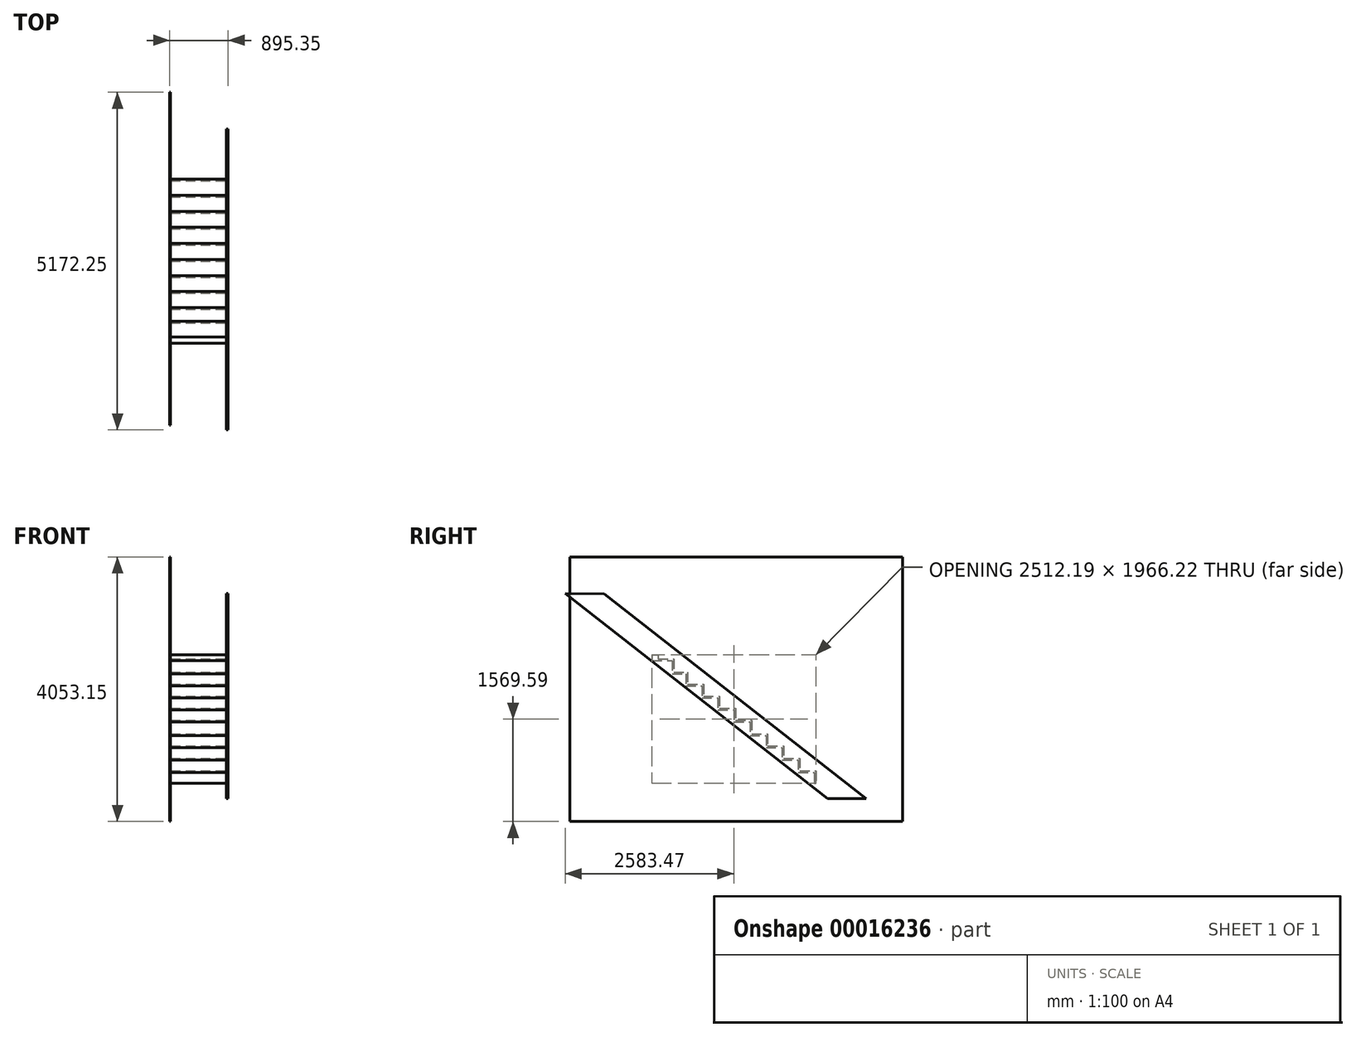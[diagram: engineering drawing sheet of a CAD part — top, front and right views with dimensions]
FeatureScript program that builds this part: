
annotation { "Feature Type Name" : "Feature", "Feature Type Description" : "" }
export const myFeature = defineFeature(function(context is Context, id is Id, definition is map)
    precondition{}
    {
        {
            var Q0;
            Q0=qCreatedBy(makeId("Right.planeOp"),FACE);
            var sketch = newSketch(context, id + "F0", { "sketchPlane" : qUnion([Q0])});
            skLineSegment(sketch, "E0", {"start": v(-670.58, 605.84) * mm, "end": v(-454.68, 605.84) * mm});
            skLineSegment(sketch, "E1", {"start": v(-454.68, 605.84) * mm, "end": v(-454.68, 402.64) * mm});
            skLineSegment(sketch, "E2", {"start": v(-454.68, 402.64) * mm, "end": v(-245.13, 402.64) * mm});
            skLineSegment(sketch, "E3", {"start": v(-245.13, 402.64) * mm, "end": v(-245.13, 218.5) * mm});
            skLineSegment(sketch, "E4", {"start": v(-245.13, 218.5) * mm, "end": v(0.68, 218.5) * mm});
            skLineSegment(sketch, "E5", {"start": v(0.68, 218.5) * mm, "end": v(0.68, 34.34) * mm});
            skLineSegment(sketch, "E6", {"start": v(0.68, 34.34) * mm, "end": v(246.48, 34.34) * mm});
            skLineSegment(sketch, "E7", {"start": v(246.48, 34.34) * mm, "end": v(246.48, -149.8) * mm});
            skLineSegment(sketch, "E8", {"start": v(246.48, -149.8) * mm, "end": v(492.28, -149.8) * mm});
            skLineSegment(sketch, "E9", {"start": v(492.28, -149.8) * mm, "end": v(492.28, -333.96) * mm});
            skLineSegment(sketch, "E10", {"start": v(492.28, -333.96) * mm, "end": v(738.09, -333.96) * mm});
            skLineSegment(sketch, "E11", {"start": v(738.09, -333.96) * mm, "end": v(738.09, -543.18) * mm});
            skLineSegment(sketch, "E12", {"start": v(-772.64, 715.75) * mm, "end": v(-772.64, -717.04) * mm, "construction": true});
            skLineSegment(sketch, "E13", {"start": v(-833.07, 660.16) * mm, "end": v(734.14, -564.28) * mm});
            skLineSegment(sketch, "E14.0", {"start": v(763.16, -308.88) * mm, "end": v(763.16, -518.1) * mm});
            skLineSegment(sketch, "E14.1", {"start": v(517.36, -308.88) * mm, "end": v(763.16, -308.88) * mm});
            skLineSegment(sketch, "E14.2", {"start": v(-220.05, 427.72) * mm, "end": v(-220.05, 243.57) * mm});
            skLineSegment(sketch, "E14.3", {"start": v(-429.6, 427.72) * mm, "end": v(-220.05, 427.72) * mm});
            skLineSegment(sketch, "E14.4", {"start": v(-429.6, 630.92) * mm, "end": v(-429.6, 427.72) * mm});
            skLineSegment(sketch, "E14.5", {"start": v(-670.58, 630.92) * mm, "end": v(-429.6, 630.92) * mm});
            skLineSegment(sketch, "E14.6", {"start": v(-220.05, 243.57) * mm, "end": v(25.75, 243.57) * mm});
            skLineSegment(sketch, "E14.7", {"start": v(25.75, 243.57) * mm, "end": v(25.75, 59.42) * mm});
            skLineSegment(sketch, "E14.8", {"start": v(25.75, 59.42) * mm, "end": v(271.55, 59.42) * mm});
            skLineSegment(sketch, "E14.9", {"start": v(271.55, 59.42) * mm, "end": v(271.55, -124.73) * mm});
            skLineSegment(sketch, "E14.10", {"start": v(271.55, -124.73) * mm, "end": v(517.36, -124.73) * mm});
            skLineSegment(sketch, "E14.11", {"start": v(517.36, -124.73) * mm, "end": v(517.36, -308.88) * mm});
            skLineSegment(sketch, "E15.bottom", {"start": v(-765.83, 694.74) * mm, "end": v(-670.58, 694.74) * mm});
            skLineSegment(sketch, "E15.top", {"start": v(-765.83, 605.84) * mm, "end": v(-670.58, 605.84) * mm});
            skLineSegment(sketch, "E15.left", {"start": v(-765.83, 694.74) * mm, "end": v(-765.83, 605.84) * mm});
            skLineSegment(sketch, "E15.right", {"start": v(-670.58, 694.74) * mm, "end": v(-670.58, 630.92) * mm});
            skLineSegment(sketch, "E16", {"start": v(763.16, -518.1) * mm, "end": v(1008.96, -518.1) * mm});
            skLineSegment(sketch, "E17", {"start": v(1008.96, -518.1) * mm, "end": v(1008.96, -697.8) * mm});
            skLineSegment(sketch, "E18", {"start": v(1008.96, -697.8) * mm, "end": v(1254.76, -697.8) * mm});
            skLineSegment(sketch, "E19", {"start": v(1254.76, -697.8) * mm, "end": v(1254.76, -887.85) * mm});
            skLineSegment(sketch, "E20", {"start": v(1254.76, -887.85) * mm, "end": v(1500.56, -887.85) * mm});
            skLineSegment(sketch, "E21", {"start": v(1500.56, -887.85) * mm, "end": v(1500.56, -1083.23) * mm});
            skLineSegment(sketch, "E22", {"start": v(1500.56, -1083.23) * mm, "end": v(1746.37, -1083.23) * mm});
            skLineSegment(sketch, "E23", {"start": v(1746.37, -1083.23) * mm, "end": v(1746.37, -1271.48) * mm});
            skLineSegment(sketch, "E24.0", {"start": v(1721.3, -1108.3) * mm, "end": v(1721.3, -1271.48) * mm});
            skLineSegment(sketch, "E24.1", {"start": v(1475.5, -1108.3) * mm, "end": v(1721.3, -1108.3) * mm});
            skLineSegment(sketch, "E24.2", {"start": v(1475.5, -912.92) * mm, "end": v(1475.5, -1108.3) * mm});
            skLineSegment(sketch, "E24.3", {"start": v(1229.7, -912.92) * mm, "end": v(1475.5, -912.92) * mm});
            skLineSegment(sketch, "E24.4", {"start": v(738.09, -543.18) * mm, "end": v(983.89, -543.18) * mm});
            skLineSegment(sketch, "E24.5", {"start": v(983.89, -543.18) * mm, "end": v(983.89, -722.86) * mm});
            skLineSegment(sketch, "E24.6", {"start": v(983.89, -722.86) * mm, "end": v(1229.7, -722.86) * mm});
            skLineSegment(sketch, "E24.7", {"start": v(1229.7, -722.86) * mm, "end": v(1229.7, -912.92) * mm});
            skLineSegment(sketch, "E25", {"start": v(1721.3, -1271.48) * mm, "end": v(1746.37, -1271.48) * mm});
            skSolve(sketch);
        }
        {
            var Q0;
            {var subQ5=sQuery(id+"F0.wireOp",EDGE,"E0");Q0=makeQuery(id+"F0.imprint","IMPRINT",FACE,{"disambiguationData":[TD([[makeQuery(id+"F0.imprint","IMPRINT",EDGE,{"derivedFrom":subQ5}),1.0]])]});}
            extrude(context, id + "F1", {"entities" : qUnion([Q0]), "oppositeDirection" : true, "depth" : 857.25 * mm});
        }
        {
            var Q0;
            Q0=makeQuery(id+"F1.opExtrude","CAP_FACE",FACE,{"disambiguationData":[OSD([sQuery(id+"F0.wireOp",EDGE,"E0"),sQuery(id+"F0.wireOp",EDGE,"E1"),sQuery(id+"F0.wireOp",EDGE,"E2"),sQuery(id+"F0.wireOp",EDGE,"E3"),sQuery(id+"F0.wireOp",EDGE,"E4"),sQuery(id+"F0.wireOp",EDGE,"E5"),sQuery(id+"F0.wireOp",EDGE,"E6"),sQuery(id+"F0.wireOp",EDGE,"E7"),sQuery(id+"F0.wireOp",EDGE,"E8"),sQuery(id+"F0.wireOp",EDGE,"E9"),sQuery(id+"F0.wireOp",EDGE,"E10"),sQuery(id+"F0.wireOp",EDGE,"E11"),sQuery(id+"F0.wireOp",EDGE,"E13"),sQuery(id+"F0.wireOp",EDGE,"E14.0"),sQuery(id+"F0.wireOp",EDGE,"E14.1"),sQuery(id+"F0.wireOp",EDGE,"E14.2"),sQuery(id+"F0.wireOp",EDGE,"E14.3"),sQuery(id+"F0.wireOp",EDGE,"E14.4"),sQuery(id+"F0.wireOp",EDGE,"E14.5"),sQuery(id+"F0.wireOp",EDGE,"E14.6"),sQuery(id+"F0.wireOp",EDGE,"E14.7"),sQuery(id+"F0.wireOp",EDGE,"E14.8"),sQuery(id+"F0.wireOp",EDGE,"E14.9"),sQuery(id+"F0.wireOp",EDGE,"E14.10"),sQuery(id+"F0.wireOp",EDGE,"E14.11"),sQuery(id+"F0.wireOp",EDGE,"9PQy3bws-XsBZ-Fjjl-eCXk-oW0PG22LN1TX"),sQuery(id+"F0.wireOp",EDGE,"E15.bottom"),sQuery(id+"F0.wireOp",EDGE,"E15.top"),sQuery(id+"F0.wireOp",EDGE,"E15.left"),sQuery(id+"F0.wireOp",EDGE,"E15.right")])],"isStart":true});
            var sketch = newSketch(context, id + "F2", { "sketchPlane" : qUnion([Q0])});
            skLineSegment(sketch, "E26", {"start": v(-2093.2, 1635.6) * mm, "end": v(1928.08, -1506.16) * mm});
            skLineSegment(sketch, "E27", {"start": v(-1498.62, 1630.66) * mm, "end": v(2516.33, -1506.16) * mm});
            skLineSegment(sketch, "E28", {"start": v(-1177.85, 846.3) * mm, "end": v(-1177.85, -739.9) * mm, "construction": true});
            skPoint(sketch, "E29.orphan", {"position": v(-1008.65, 788.26) * mm});
            skPoint(sketch, "E30.orphan", {"position": v(-695.72, 1003.36) * mm});
            skLineSegment(sketch, "E31", {"start": v(-2093.2, 1635.6) * mm, "end": v(-1498.62, 1630.66) * mm});
            skLineSegment(sketch, "E32", {"start": v(1928.08, -1506.16) * mm, "end": v(2516.33, -1506.16) * mm});
            skSolve(sketch);
        }
        {
            var Q0;
            Q0=makeQuery(id+"F2.imprint","IMPRINT",FACE,{"disambiguationData":[TD([[makeQuery(id+"F2.imprint","IMPRINT",EDGE,{"derivedFrom":sQuery(id+"F2.wireOp",EDGE,"E26")}),1.0]])]});
            var Q1;
            Q1=makeQuery(id+"F2.imprint","IMPRINT",FACE,{"disambiguationData":[TD([[makeQuery(id+"F2.imprint","IMPRINT",EDGE,{"derivedFrom":makeQuery(id+"F1.opExtrude","CAP_EDGE",EDGE,{"disambiguationData":[OSD([sQuery(id+"F0.wireOp",EDGE,"E1")])],"isStart":true})}),1.0]])]});
            extrude(context, id + "F3", {"entities" : qUnion([Q0, Q1]), "operationType" : NewBodyOperationType.ADD, "depth" : 25.4 * mm});
        }
        {
            var Q0;
            Q0=makeQuery(id+"F1.opExtrude","CAP_FACE",FACE,{"disambiguationData":[OSD([sQuery(id+"F0.wireOp",EDGE,"E0"),sQuery(id+"F0.wireOp",EDGE,"E1"),sQuery(id+"F0.wireOp",EDGE,"E2"),sQuery(id+"F0.wireOp",EDGE,"E3"),sQuery(id+"F0.wireOp",EDGE,"E4"),sQuery(id+"F0.wireOp",EDGE,"E5"),sQuery(id+"F0.wireOp",EDGE,"E6"),sQuery(id+"F0.wireOp",EDGE,"E7"),sQuery(id+"F0.wireOp",EDGE,"E8"),sQuery(id+"F0.wireOp",EDGE,"E9"),sQuery(id+"F0.wireOp",EDGE,"E10"),sQuery(id+"F0.wireOp",EDGE,"E11"),sQuery(id+"F0.wireOp",EDGE,"E13"),sQuery(id+"F0.wireOp",EDGE,"E14.0"),sQuery(id+"F0.wireOp",EDGE,"E14.1"),sQuery(id+"F0.wireOp",EDGE,"E14.2"),sQuery(id+"F0.wireOp",EDGE,"E14.3"),sQuery(id+"F0.wireOp",EDGE,"E14.4"),sQuery(id+"F0.wireOp",EDGE,"E14.5"),sQuery(id+"F0.wireOp",EDGE,"E14.6"),sQuery(id+"F0.wireOp",EDGE,"E14.7"),sQuery(id+"F0.wireOp",EDGE,"E14.8"),sQuery(id+"F0.wireOp",EDGE,"E14.9"),sQuery(id+"F0.wireOp",EDGE,"E14.10"),sQuery(id+"F0.wireOp",EDGE,"E14.11"),sQuery(id+"F0.wireOp",EDGE,"E15.bottom"),sQuery(id+"F0.wireOp",EDGE,"E15.top"),sQuery(id+"F0.wireOp",EDGE,"E15.left"),sQuery(id+"F0.wireOp",EDGE,"E15.right"),sQuery(id+"F0.wireOp",EDGE,"E16"),sQuery(id+"F0.wireOp",EDGE,"E17"),sQuery(id+"F0.wireOp",EDGE,"E18"),sQuery(id+"F0.wireOp",EDGE,"E19"),sQuery(id+"F0.wireOp",EDGE,"E20"),sQuery(id+"F0.wireOp",EDGE,"E21"),sQuery(id+"F0.wireOp",EDGE,"E22"),sQuery(id+"F0.wireOp",EDGE,"E23"),sQuery(id+"F0.wireOp",EDGE,"E24.0"),sQuery(id+"F0.wireOp",EDGE,"E24.1"),sQuery(id+"F0.wireOp",EDGE,"E24.2"),sQuery(id+"F0.wireOp",EDGE,"E24.3"),sQuery(id+"F0.wireOp",EDGE,"E24.4"),sQuery(id+"F0.wireOp",EDGE,"E24.5"),sQuery(id+"F0.wireOp",EDGE,"E24.6"),sQuery(id+"F0.wireOp",EDGE,"E24.7"),sQuery(id+"F0.wireOp",EDGE,"E25")])],"isStart":false});
            var sketch = newSketch(context, id + "F4", { "sketchPlane" : qUnion([Q0])});
            skLineSegment(sketch, "E33.bottom", {"start": v(-3079.05, 2195.2) * mm, "end": v(2025.22, 2195.2) * mm});
            skLineSegment(sketch, "E33.top", {"start": v(-3079.05, -1857.96) * mm, "end": v(2025.22, -1857.96) * mm});
            skLineSegment(sketch, "E33.left", {"start": v(-3079.05, 2195.2) * mm, "end": v(-3079.05, -1857.96) * mm});
            skLineSegment(sketch, "E33.right", {"start": v(2025.22, 2195.2) * mm, "end": v(2025.22, -1857.96) * mm});
            skSolve(sketch);
        }
        {
            var Q0;
            Q0=makeQuery(id+"F4.imprint","IMPRINT",FACE,{"disambiguationData":[TD([[makeQuery(id+"F4.imprint","IMPRINT",EDGE,{"derivedFrom":makeQuery(id+"F1.opExtrude","CAP_EDGE",EDGE,{"disambiguationData":[OSD([sQuery(id+"F0.wireOp",EDGE,"E1")])],"isStart":false})}),-1.0]])]});
            var Q1;
            Q1=makeQuery(id+"F4.imprint","IMPRINT",FACE,{"disambiguationData":[TD([[makeQuery(id+"F4.imprint","IMPRINT",EDGE,{"derivedFrom":sQuery(id+"F4.wireOp",EDGE,"E33.bottom")}),-1.0]])]});
            extrude(context, id + "F5", {"entities" : qUnion([Q0, Q1]), "operationType" : NewBodyOperationType.ADD, "depth" : 12.7 * mm});
        }
    });
